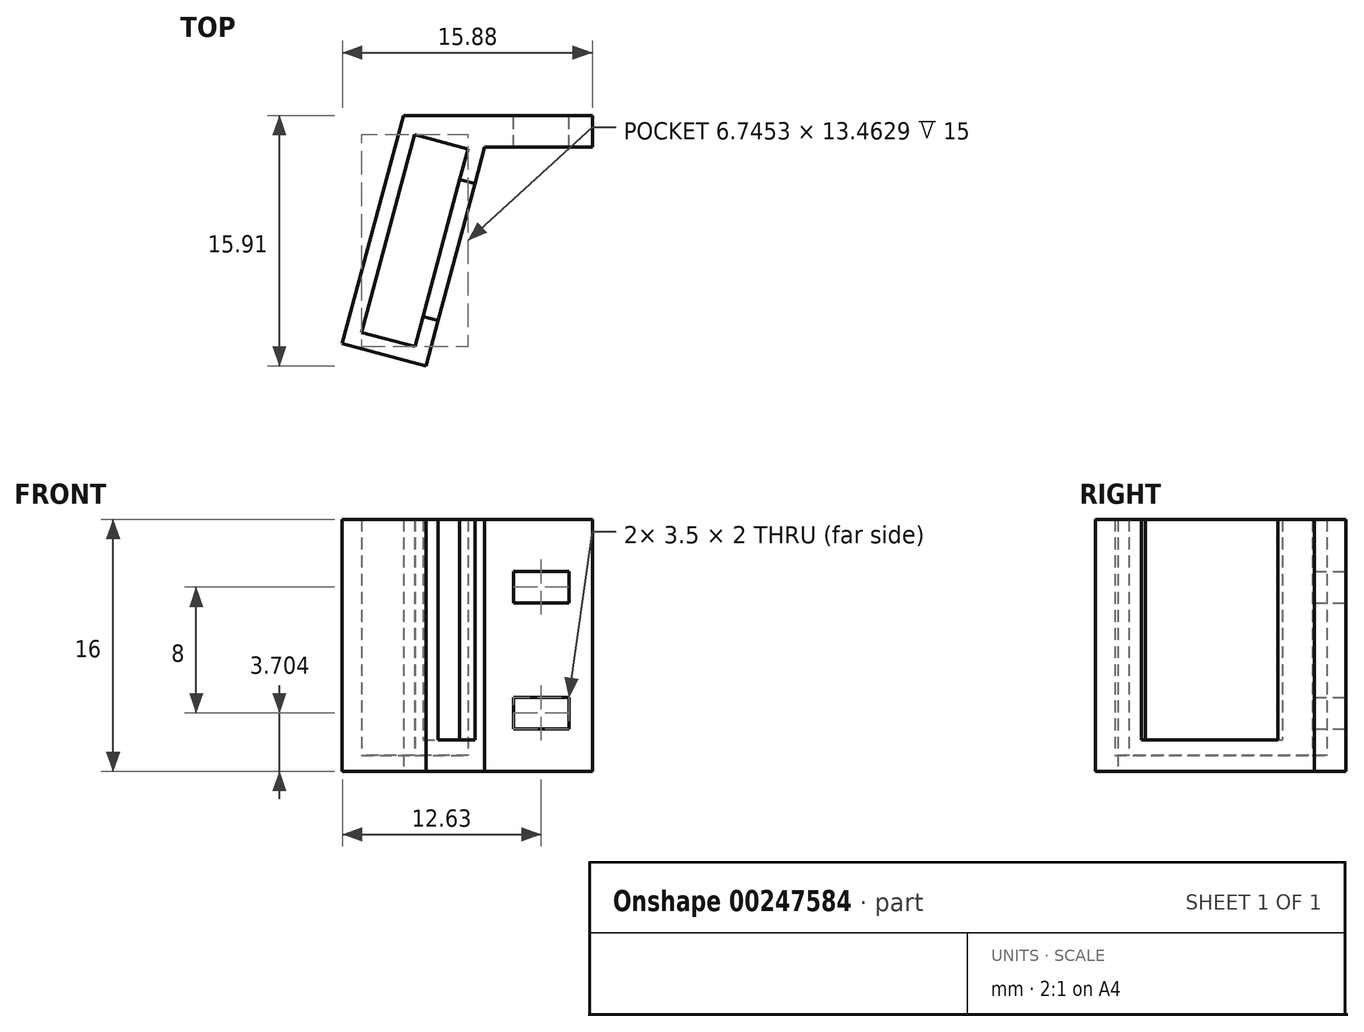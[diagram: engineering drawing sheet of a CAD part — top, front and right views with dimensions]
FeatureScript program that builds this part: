
annotation { "Feature Type Name" : "Feature", "Feature Type Description" : "" }
export const myFeature = defineFeature(function(context is Context, id is Id, definition is map)
    precondition{}
    {
        {
            var Q0;
            Q0=qCreatedBy(makeId("Top.planeOp"),FACE);
            var sketch = newSketch(context, id + "F0", { "sketchPlane" : qUnion([Q0])});
            skLineSegment(sketch, "E0.bottom", {"start": v(0, 0) * mm, "end": v(12, 0) * mm});
            skLineSegment(sketch, "E0.right", {"start": v(12, 0) * mm, "end": v(12, -2) * mm});
            skLineSegment(sketch, "E1", {"start": v(2.2, -13.01) * mm, "end": v(1.43, -15.91) * mm});
            skLineSegment(sketch, "E2", {"start": v(1.43, -15.91) * mm, "end": v(-3.88, -14.49) * mm});
            skLineSegment(sketch, "E3", {"start": v(-3.88, -14.49) * mm, "end": v(-3.1, -11.6) * mm});
            skLineSegment(sketch, "E4", {"start": v(-3.1, -11.6) * mm, "end": v(-2.14, -11.85) * mm});
            skLineSegment(sketch, "E5", {"start": v(-2.14, -11.85) * mm, "end": v(-2.66, -13.78) * mm});
            skLineSegment(sketch, "E6", {"start": v(-2.66, -13.78) * mm, "end": v(0.72, -14.69) * mm});
            skLineSegment(sketch, "E7", {"start": v(0.72, -14.69) * mm, "end": v(1.24, -12.76) * mm});
            skLineSegment(sketch, "E8", {"start": v(1.24, -12.76) * mm, "end": v(2.2, -13.01) * mm});
            skLineSegment(sketch, "E9", {"start": v(-0.78, -2.9) * mm, "end": v(0, 0) * mm});
            skLineSegment(sketch, "E10", {"start": v(0, 0) * mm, "end": v(5.31, -1.42) * mm});
            skLineSegment(sketch, "E11", {"start": v(5.31, -1.42) * mm, "end": v(4.54, -4.32) * mm});
            skLineSegment(sketch, "E12", {"start": v(4.54, -4.32) * mm, "end": v(3.57, -4.06) * mm});
            skLineSegment(sketch, "E13", {"start": v(3.57, -4.06) * mm, "end": v(4.09, -2.13) * mm});
            skLineSegment(sketch, "E14", {"start": v(4.09, -2.13) * mm, "end": v(0.7, -1.22) * mm});
            skLineSegment(sketch, "E15", {"start": v(0.7, -1.22) * mm, "end": v(0.19, -3.16) * mm});
            skLineSegment(sketch, "E16", {"start": v(0.19, -3.16) * mm, "end": v(-0.78, -2.9) * mm});
            skLineSegment(sketch, "E17", {"start": v(-0.78, -2.9) * mm, "end": v(-3.1, -11.6) * mm});
            skLineSegment(sketch, "E18", {"start": v(4.54, -4.32) * mm, "end": v(2.2, -13.01) * mm});
            skLineSegment(sketch, "E19", {"start": v(1.24, -12.76) * mm, "end": v(3.57, -4.06) * mm});
            skLineSegment(sketch, "E20", {"start": v(0.19, -3.16) * mm, "end": v(-2.14, -11.85) * mm});
            skLineSegment(sketch, "E21.0", {"start": v(0.19, -3.16) * mm, "end": v(4.54, -4.32) * mm, "construction": true});
            skLineSegment(sketch, "E22.0", {"start": v(-3.1, -11.6) * mm, "end": v(1.24, -12.76) * mm, "construction": true});
            skLineSegment(sketch, "E23", {"start": v(12, -2) * mm, "end": v(5.16, -2) * mm});
            skSolve(sketch);
        }
        {
            var Q0;
            Q0=makeQuery(id+"F0.imprint","IMPRINT",FACE,{"disambiguationData":[TD([[makeQuery(id+"F0.imprint","IMPRINT",EDGE,{"derivedFrom":sQuery(id+"F0.wireOp",EDGE,"E9")}),-1.0]])]});
            var Q1;
            Q1=makeQuery(id+"F0.imprint","IMPRINT",FACE,{"disambiguationData":[TD([[makeQuery(id+"F0.imprint","IMPRINT",EDGE,{"derivedFrom":sQuery(id+"F0.wireOp",EDGE,"E1")}),-1.0]])]});
            var Q2;
            Q2=makeQuery(id+"F0.imprint","IMPRINT",FACE,{"disambiguationData":[TD([[makeQuery(id+"F0.imprint","IMPRINT",EDGE,{"derivedFrom":sQuery(id+"F0.wireOp",EDGE,"E4")}),1.0]])]});
            var Q3;
            Q3=makeQuery(id+"F0.imprint","IMPRINT",FACE,{"disambiguationData":[TD([[makeQuery(id+"F0.imprint","IMPRINT",EDGE,{"derivedFrom":sQuery(id+"F0.wireOp",EDGE,"E0.bottom")}),-1.0]])]});
            extrude(context, id + "F1", {"entities" : qUnion([Q0, Q1, Q2, Q3]), "depth" : 16 * mm, "offsetDistance" : 25 * mm});
        }
        {
            var Q0;
            Q0=makeQuery(id+"F0.imprint","IMPRINT",FACE,{"disambiguationData":[TD([[makeQuery(id+"F0.imprint","IMPRINT",EDGE,{"derivedFrom":sQuery(id+"F0.wireOp",EDGE,"E5")}),1.0]])]});
            extrude(context, id + "F2", {"entities" : qUnion([Q0]), "operationType" : NewBodyOperationType.ADD, "depth" : 1 * mm, "offsetDistance" : 25 * mm});
        }
        {
            var Q0;
            Q0=makeQuery(id+"F0.imprint","IMPRINT",FACE,{"disambiguationData":[TD([[makeQuery(id+"F0.imprint","IMPRINT",EDGE,{"derivedFrom":sQuery(id+"F0.wireOp",EDGE,"E8")}),1.0]])]});
            extrude(context, id + "F3", {"entities" : qUnion([Q0]), "operationType" : NewBodyOperationType.ADD, "depth" : 2 * mm, "offsetDistance" : 25 * mm});
        }
        {
            var Q0;
            Q0=qCreatedBy(makeId("Front.planeOp"),FACE);
            var sketch = newSketch(context, id + "F4", { "sketchPlane" : qUnion([Q0])});
            skLineSegment(sketch, "E24.bottom", {"start": v(18, 10.7) * mm, "end": v(14.5, 10.7) * mm});
            skLineSegment(sketch, "E24.top", {"start": v(18, 12.7) * mm, "end": v(14.5, 12.7) * mm});
            skLineSegment(sketch, "E24.left", {"start": v(18, 10.7) * mm, "end": v(18, 12.7) * mm});
            skLineSegment(sketch, "E24.right", {"start": v(14.5, 10.7) * mm, "end": v(14.5, 12.7) * mm});
            skLineSegment(sketch, "E25.bottom", {"start": v(18, 2.7) * mm, "end": v(14.5, 2.7) * mm});
            skLineSegment(sketch, "E25.top", {"start": v(18, 4.7) * mm, "end": v(14.5, 4.7) * mm});
            skLineSegment(sketch, "E25.left", {"start": v(18, 2.7) * mm, "end": v(18, 4.7) * mm});
            skLineSegment(sketch, "E25.right", {"start": v(14.5, 2.7) * mm, "end": v(14.5, 4.7) * mm});
            skSolve(sketch);
        }
        {
            var Q0;
            Q0 = qSketchRegion(id + "F4", true);
            extrude(context, id + "F5", {"entities" : qUnion([Q0]), "operationType" : NewBodyOperationType.ADD, "endBound" : BoundingType.SYMMETRIC, "depth" : 5 * mm, "offsetDistance" : 25 * mm});
        }
        {
            var Q0;
            Q0=makeQuery(id+"F5.opExtrude","SWEPT_BODY",BODY,{"disambiguationData":[OSD([sQuery(id+"F4.wireOp",EDGE,"E24.bottom"),sQuery(id+"F4.wireOp",EDGE,"E24.top"),sQuery(id+"F4.wireOp",EDGE,"E24.left"),sQuery(id+"F4.wireOp",EDGE,"E24.right")])]});
            var Q1;
            Q1=makeQuery(id+"F5.opExtrude","SWEPT_BODY",BODY,{"disambiguationData":[OSD([sQuery(id+"F4.wireOp",EDGE,"E25.bottom"),sQuery(id+"F4.wireOp",EDGE,"E25.top"),sQuery(id+"F4.wireOp",EDGE,"E25.left"),sQuery(id+"F4.wireOp",EDGE,"E25.right")])]});
            transform(context, id + "F6", {"entities" : qUnion([Q0, Q1]), "transformType" : TransformType.TRANSLATION_3D, "dx" : -7.5 * mm, "dy" : 0 * mm, "dz" : 0 * mm, "makeCopy" : false});
        }
        {
            var Q0;
            Q0=makeQuery(id+"F5.opExtrude","SWEPT_BODY",BODY,{"disambiguationData":[OSD([sQuery(id+"F4.wireOp",EDGE,"E24.bottom"),sQuery(id+"F4.wireOp",EDGE,"E24.top"),sQuery(id+"F4.wireOp",EDGE,"E24.left"),sQuery(id+"F4.wireOp",EDGE,"E24.right")])]});
            var Q1;
            Q1=makeQuery(id+"F5.opExtrude","SWEPT_BODY",BODY,{"disambiguationData":[OSD([sQuery(id+"F4.wireOp",EDGE,"E25.bottom"),sQuery(id+"F4.wireOp",EDGE,"E25.top"),sQuery(id+"F4.wireOp",EDGE,"E25.left"),sQuery(id+"F4.wireOp",EDGE,"E25.right")])]});
            var Q2;
            Q2=makeQuery(id+"F1.opExtrude","SWEPT_BODY",BODY,{"disambiguationData":[OSD([sQuery(id+"F0.wireOp",EDGE,"E0.bottom"),sQuery(id+"F0.wireOp",EDGE,"E0.right"),sQuery(id+"F0.wireOp",EDGE,"E1"),sQuery(id+"F0.wireOp",EDGE,"E2"),sQuery(id+"F0.wireOp",EDGE,"E3"),sQuery(id+"F0.wireOp",EDGE,"E5"),sQuery(id+"F0.wireOp",EDGE,"E6"),sQuery(id+"F0.wireOp",EDGE,"E7"),sQuery(id+"F0.wireOp",EDGE,"E8"),sQuery(id+"F0.wireOp",EDGE,"E9"),sQuery(id+"F0.wireOp",EDGE,"E11"),sQuery(id+"F0.wireOp",EDGE,"E12"),sQuery(id+"F0.wireOp",EDGE,"E13"),sQuery(id+"F0.wireOp",EDGE,"E14"),sQuery(id+"F0.wireOp",EDGE,"E15"),sQuery(id+"F0.wireOp",EDGE,"E17"),sQuery(id+"F0.wireOp",EDGE,"E20"),sQuery(id+"F0.wireOp",EDGE,"5YgbU1Aj-dg0T-XtkC-uFpF-ygSdP0D5SG6H")])]});
            booleanBodies(context, id + "F7", {"operationType" : BooleanOperationType.SUBTRACTION, "tools" : qUnion([Q0, Q1]), "targets" : qUnion([Q2])});
        }
    });
